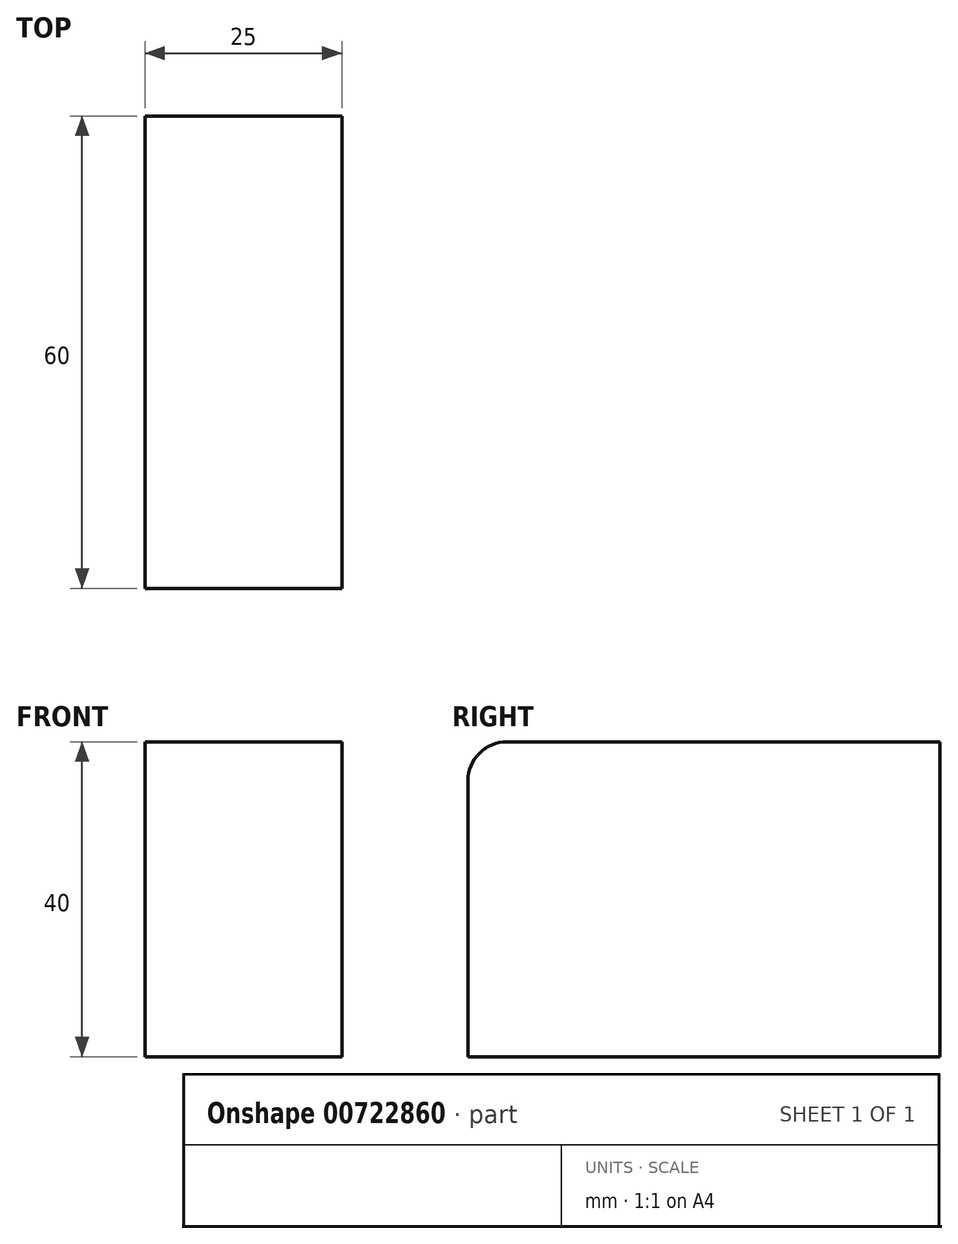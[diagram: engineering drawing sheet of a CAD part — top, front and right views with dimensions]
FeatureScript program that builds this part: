
annotation { "Feature Type Name" : "Feature", "Feature Type Description" : "" }
export const myFeature = defineFeature(function(context is Context, id is Id, definition is map)
    precondition{}
    {
        {
            var Q0;
            Q0=qCreatedBy(makeId("Right.planeOp"),FACE);
            var sketch = newSketch(context, id + "F0", { "sketchPlane" : qUnion([Q0])});
            skLineSegment(sketch, "E0.bottom", {"start": v(-30, -20) * mm, "end": v(30, -20) * mm});
            skLineSegment(sketch, "E0.top", {"start": v(-30, 20) * mm, "end": v(30, 20) * mm});
            skLineSegment(sketch, "E0.left", {"start": v(-30, -20) * mm, "end": v(-30, 20) * mm});
            skLineSegment(sketch, "E0.right", {"start": v(30, -20) * mm, "end": v(30, 20) * mm});
            skPoint(sketch, "E0.middle", {"position": v(0, 0) * mm});
            skSolve(sketch);
        }
        {
            var Q0;
            Q0 = qSketchRegion(id + "F0", true);
            extrude(context, id + "F1", {"entities" : qUnion([Q0]), "depth" : 25 * mm, "offsetDistance" : 25 * mm});
        }
        {
            var Q0;
            Q0=makeQuery(id+"F1.opExtrude","SWEPT_EDGE",EDGE,{"disambiguationData":[OSD([sQuery(id+"F0.wireOp",EDGE,"E0.top"),sQuery(id+"F0.wireOp",EDGE,"E0.left")])]});
            fillet(context, id + "F2", {"entities" : qUnion([Q0]), "radius" : 5 * mm, "tangentPropagation" : true, "allowEdgeOverflow" : false});
        }
    });
